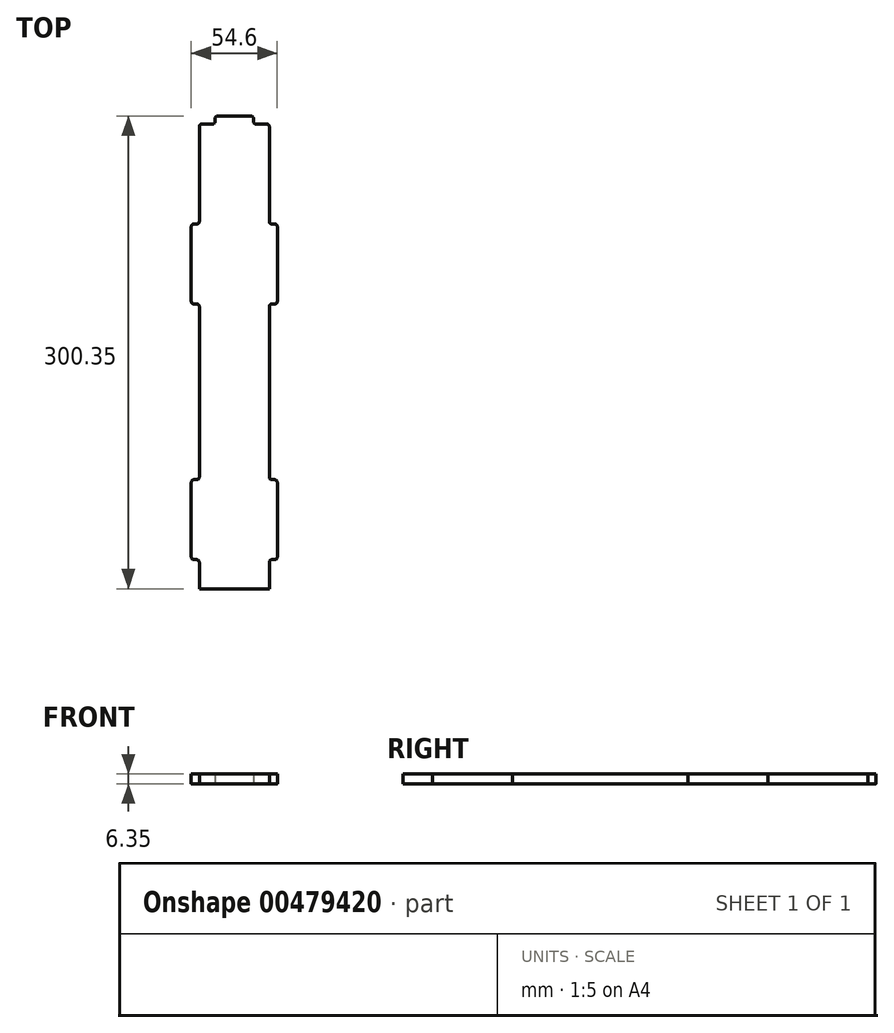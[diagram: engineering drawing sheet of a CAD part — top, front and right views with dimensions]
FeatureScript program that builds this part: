
annotation { "Feature Type Name" : "Feature", "Feature Type Description" : "" }
export const myFeature = defineFeature(function(context is Context, id is Id, definition is map)
    precondition{}
    {
        {
            var Q0;
            Q0=qCreatedBy(makeId("Top.planeOp"),FACE);
            var sketch = newSketch(context, id + "F0", { "sketchPlane" : qUnion([Q0])});
            skLineSegment(sketch, "E0", {"start": v(0, 0) * mm, "end": v(22.23, 0) * mm});
            skLineSegment(sketch, "E1", {"start": v(22.23, 0) * mm, "end": v(22.23, 16.94) * mm});
            skLineSegment(sketch, "E2", {"start": v(23.83, 18.54) * mm, "end": v(25.7, 18.54) * mm});
            skLineSegment(sketch, "E3", {"start": v(27.3, 20.14) * mm, "end": v(27.3, 67.74) * mm});
            skLineSegment(sketch, "E4", {"start": v(25.7, 69.34) * mm, "end": v(23.83, 69.34) * mm});
            skLineSegment(sketch, "E5", {"start": v(22.23, 70.94) * mm, "end": v(22.23, 179.37) * mm});
            skLineSegment(sketch, "E6", {"start": v(23.83, 180.97) * mm, "end": v(25.7, 180.97) * mm});
            skLineSegment(sketch, "E7", {"start": v(27.3, 182.58) * mm, "end": v(27.3, 230.17) * mm});
            skLineSegment(sketch, "E8", {"start": v(25.7, 231.78) * mm, "end": v(23.83, 231.78) * mm});
            skLineSegment(sketch, "E9", {"start": v(22.22, 233.38) * mm, "end": v(22.22, 293.67) * mm});
            skLineSegment(sketch, "E10", {"start": v(20.62, 295.28) * mm, "end": v(13.8, 295.28) * mm});
            skLineSegment(sketch, "E11", {"start": v(12.2, 296.88) * mm, "end": v(12.2, 298.75) * mm});
            skLineSegment(sketch, "E12", {"start": v(10.6, 300.36) * mm, "end": v(0, 300.36) * mm});
            skLineSegment(sketch, "E13", {"start": v(0, 300.36) * mm, "end": v(0, 0) * mm});
            skPoint(sketch, "E14.visualSharp", {"position": v(22.22, 295.28) * mm});
            skArc(sketch, "E14.filletArc", {"start": v(22.22, 293.67) * mm, "mid": v(21.76, 294.8) * mm, "end": v(20.62, 295.28) * mm});
            skPoint(sketch, "E15.visualSharp", {"position": v(12.2, 300.36) * mm});
            skArc(sketch, "E15.filletArc", {"start": v(12.2, 298.75) * mm, "mid": v(11.72, 299.89) * mm, "end": v(10.6, 300.36) * mm});
            skPoint(sketch, "E16.visualSharp", {"position": v(12.2, 295.28) * mm});
            skArc(sketch, "E16.filletArc", {"start": v(12.2, 296.88) * mm, "mid": v(12.66, 295.74) * mm, "end": v(13.8, 295.28) * mm});
            skPoint(sketch, "E17.visualSharp", {"position": v(22.23, 231.78) * mm});
            skArc(sketch, "E17.filletArc", {"start": v(22.22, 233.38) * mm, "mid": v(22.7, 232.24) * mm, "end": v(23.83, 231.78) * mm});
            skPoint(sketch, "E18.visualSharp", {"position": v(27.3, 231.78) * mm});
            skArc(sketch, "E18.filletArc", {"start": v(27.3, 230.17) * mm, "mid": v(26.84, 231.3) * mm, "end": v(25.7, 231.78) * mm});
            skPoint(sketch, "E19.visualSharp", {"position": v(27.3, 180.97) * mm});
            skArc(sketch, "E19.filletArc", {"start": v(25.7, 180.97) * mm, "mid": v(26.84, 181.44) * mm, "end": v(27.3, 182.58) * mm});
            skPoint(sketch, "E20.visualSharp", {"position": v(22.23, 180.97) * mm});
            skArc(sketch, "E20.filletArc", {"start": v(23.83, 180.97) * mm, "mid": v(22.7, 180.5) * mm, "end": v(22.23, 179.37) * mm});
            skPoint(sketch, "E21.visualSharp", {"position": v(22.23, 69.34) * mm});
            skArc(sketch, "E21.filletArc", {"start": v(22.23, 70.94) * mm, "mid": v(22.7, 69.81) * mm, "end": v(23.83, 69.34) * mm});
            skPoint(sketch, "E22.visualSharp", {"position": v(27.3, 69.34) * mm});
            skArc(sketch, "E22.filletArc", {"start": v(27.3, 67.74) * mm, "mid": v(26.84, 68.87) * mm, "end": v(25.7, 69.34) * mm});
            skPoint(sketch, "E23.visualSharp", {"position": v(27.3, 18.54) * mm});
            skArc(sketch, "E23.filletArc", {"start": v(25.7, 18.54) * mm, "mid": v(26.84, 19.01) * mm, "end": v(27.3, 20.14) * mm});
            skPoint(sketch, "E24.visualSharp", {"position": v(22.23, 18.54) * mm});
            skArc(sketch, "E24.filletArc", {"start": v(23.83, 18.54) * mm, "mid": v(22.7, 18.07) * mm, "end": v(22.23, 16.94) * mm});
            skSolve(sketch);
        }
        {
            var Q0;
            Q0 = qSketchRegion(id + "F0", true);
            extrude(context, id + "F1", {"entities" : qUnion([Q0]), "depth" : 6.35 * mm, "offsetDistance" : 25.4 * mm});
        }
        {
            var Q0;
            Q0=makeQuery(id+"F1.opExtrude","SWEPT_BODY",BODY,{"disambiguationData":[OSD([sQuery(id+"F0.wireOp",EDGE,"E0"),sQuery(id+"F0.wireOp",EDGE,"E1"),sQuery(id+"F0.wireOp",EDGE,"E2"),sQuery(id+"F0.wireOp",EDGE,"E3"),sQuery(id+"F0.wireOp",EDGE,"E4"),sQuery(id+"F0.wireOp",EDGE,"E5"),sQuery(id+"F0.wireOp",EDGE,"E6"),sQuery(id+"F0.wireOp",EDGE,"E7"),sQuery(id+"F0.wireOp",EDGE,"E8"),sQuery(id+"F0.wireOp",EDGE,"E9"),sQuery(id+"F0.wireOp",EDGE,"E10"),sQuery(id+"F0.wireOp",EDGE,"E11"),sQuery(id+"F0.wireOp",EDGE,"E12"),sQuery(id+"F0.wireOp",EDGE,"E13"),sQuery(id+"F0.wireOp",EDGE,"E14.filletArc"),sQuery(id+"F0.wireOp",EDGE,"E15.filletArc"),sQuery(id+"F0.wireOp",EDGE,"E16.filletArc"),sQuery(id+"F0.wireOp",EDGE,"E17.filletArc"),sQuery(id+"F0.wireOp",EDGE,"E18.filletArc"),sQuery(id+"F0.wireOp",EDGE,"E19.filletArc"),sQuery(id+"F0.wireOp",EDGE,"E20.filletArc"),sQuery(id+"F0.wireOp",EDGE,"E21.filletArc"),sQuery(id+"F0.wireOp",EDGE,"E22.filletArc"),sQuery(id+"F0.wireOp",EDGE,"E23.filletArc"),sQuery(id+"F0.wireOp",EDGE,"E24.filletArc")])]});
            var Q1;
            Q1=makeQuery(id+"F1.opExtrude","SWEPT_FACE",FACE,{"disambiguationData":[OSD([sQuery(id+"F0.wireOp",EDGE,"E13")])]});
            mirror(context, id + "F2", {"operationType" : NewBodyOperationType.ADD, "entities" : qUnion([Q0]), "mirrorPlane" : qUnion([Q1])});
        }
    });
